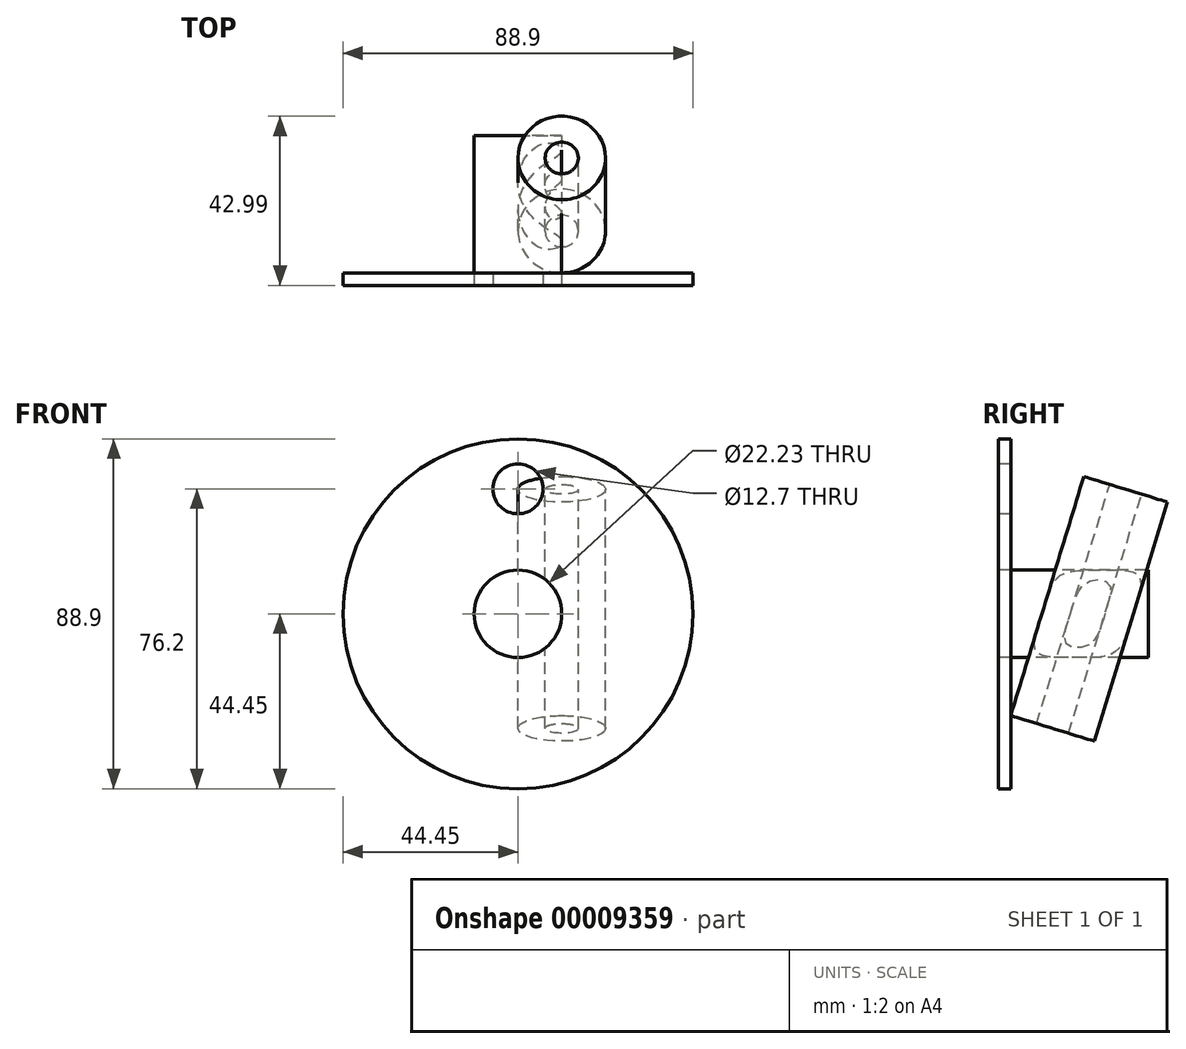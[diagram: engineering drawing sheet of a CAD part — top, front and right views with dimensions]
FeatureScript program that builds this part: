
annotation { "Feature Type Name" : "Feature", "Feature Type Description" : "" }
export const myFeature = defineFeature(function(context is Context, id is Id, definition is map)
    precondition{}
    {
        {
            var Q0;
            Q0=qCreatedBy(makeId("Front.planeOp"),FACE);
            var sketch = newSketch(context, id + "F0", { "sketchPlane" : qUnion([Q0])});
            skCircle(sketch, "E0", {"center": v(0, 0) * mm, "radius": 44.45 * mm});
            skCircle(sketch, "E1", {"center": v(0, 0) * mm, "radius": 11.11 * mm});
            skCircle(sketch, "E2", {"center": v(0, 31.75) * mm, "radius": 6.35 * mm});
            skSolve(sketch);
        }
        {
            var Q0;
            Q0 = qSketchRegion(id + "F0", true);
            extrude(context, id + "F1", {"entities" : qUnion([Q0]), "oppositeDirection" : true, "depth" : 3.17 * mm});
        }
        {
            var Q0;
            Q0=makeQuery(id+"F1.opExtrude","CAP_FACE",FACE,{"disambiguationData":[OSD([sQuery(id+"F0.wireOp",EDGE,"E0"),sQuery(id+"F0.wireOp",EDGE,"E1"),sQuery(id+"F0.wireOp",EDGE,"E2")])],"isStart":true});
            var sketch = newSketch(context, id + "F2", { "sketchPlane" : qUnion([Q0])});
            skCircle(sketch, "E3", {"center": v(0, 0) * mm, "radius": 11.11 * mm});
            skLineSegment(sketch, "E4", {"start": v(0, 11.11) * mm, "end": v(0, -11.11) * mm, "construction": true});
            skLineSegment(sketch, "E5", {"start": v(-11.11, 0) * mm, "end": v(11.11, 0) * mm, "construction": true});
            skSolve(sketch);
        }
        {
            var Q0;
            Q0 = qSketchRegion(id + "F2", true);
            extrude(context, id + "F3", {"entities" : qUnion([Q0]), "oppositeDirection" : true, "depth" : 38.1 * mm});
        }
        {
            var Q0;
            Q0=qCreatedBy(makeId("Right.planeOp"),FACE);
            var Q1;
            Q1=sQuery(id+"F2.wireOp",VERTEX,"E5.end");
            cPlane(context, id + "F4", {"entities" : qUnion([Q0, Q1]), "cplaneType" : CPlaneType.PLANE_POINT, "offset" : 152.4 * mm, "width" : 152.4 * mm, "height" : 152.4 * mm});
        }
        {
            var Q0;
            Q0=qCreatedBy(id+"F4.planeOp",FACE);
            var sketch = newSketch(context, id + "F5", { "sketchPlane" : qUnion([Q0])});
            skLineSegment(sketch, "E6", {"start": v(0, 11.11) * mm, "end": v(14.48, 11.11) * mm, "construction": true});
            skLineSegment(sketch, "E7", {"start": v(3.18, -25.86) * mm, "end": v(21.74, 34.87) * mm, "construction": true});
            skLineSegment(sketch, "E8", {"start": v(21.74, 34.87) * mm, "end": v(43, 28.37) * mm, "construction": true});
            skSolve(sketch);
        }
        {
            var Q0;
            Q0=sQuery(id+"F5.wireOp",EDGE,"E8");
            cPlane(context, id + "F6", {"entities" : qUnion([Q0]), "cplaneType" : CPlaneType.LINE_ANGLE, "offset" : 152.4 * mm, "angle" : 0 * degree, "width" : 152.4 * mm, "height" : 152.4 * mm});
        }
        {
            var Q0;
            Q0=qCreatedBy(id+"F6.planeOp",FACE);
            var Q1;
            Q1=sQuery(id+"F5.wireOp",VERTEX,"E7.start");
            cPlane(context, id + "F7", {"entities" : qUnion([Q0, Q1]), "cplaneType" : CPlaneType.PLANE_POINT, "offset" : 152.4 * mm, "width" : 152.4 * mm, "height" : 152.4 * mm});
        }
        {
            var Q0;
            Q0=qCreatedBy(id+"F6.planeOp",FACE);
            var sketch = newSketch(context, id + "F8", { "sketchPlane" : qUnion([Q0])});
            skCircle(sketch, "E9", {"center": v(11.11, 21.7) * mm, "radius": 11.11 * mm});
            skCircle(sketch, "E10", {"center": v(11.11, 21.7) * mm, "radius": 4.22 * mm});
            skSolve(sketch);
        }
        {
            var Q0;
            Q0 = qSketchRegion(id + "F8", true);
            var Q1;
            Q1=qCreatedBy(id+"F7.planeOp",FACE);
            extrude(context, id + "F9", {"entities" : qUnion([Q0]), "endBound" : BoundingType.UP_TO_SURFACE, "oppositeDirection" : true, "endBoundEntityFace" : qUnion([Q1]), "depth" : 25.4 * mm});
        }
        {
            var Q0;
            Q0=makeQuery(id+"F3.opExtrude","SWEPT_BODY",BODY,{"disambiguationData":[OSD([sQuery(id+"F2.wireOp",EDGE,"E3")])]});
            var Q1;
            Q1=makeQuery(id+"F9.opExtrude","SWEPT_BODY",BODY,{"disambiguationData":[OSD([sQuery(id+"F8.wireOp",EDGE,"E9"),sQuery(id+"F8.wireOp",EDGE,"E10")])]});
            booleanBodies(context, id + "F10", {"operationType" : BooleanOperationType.SUBTRACTION, "tools" : qUnion([Q0]), "targets" : qUnion([Q1]), "keepTools" : true});
        }
    });
